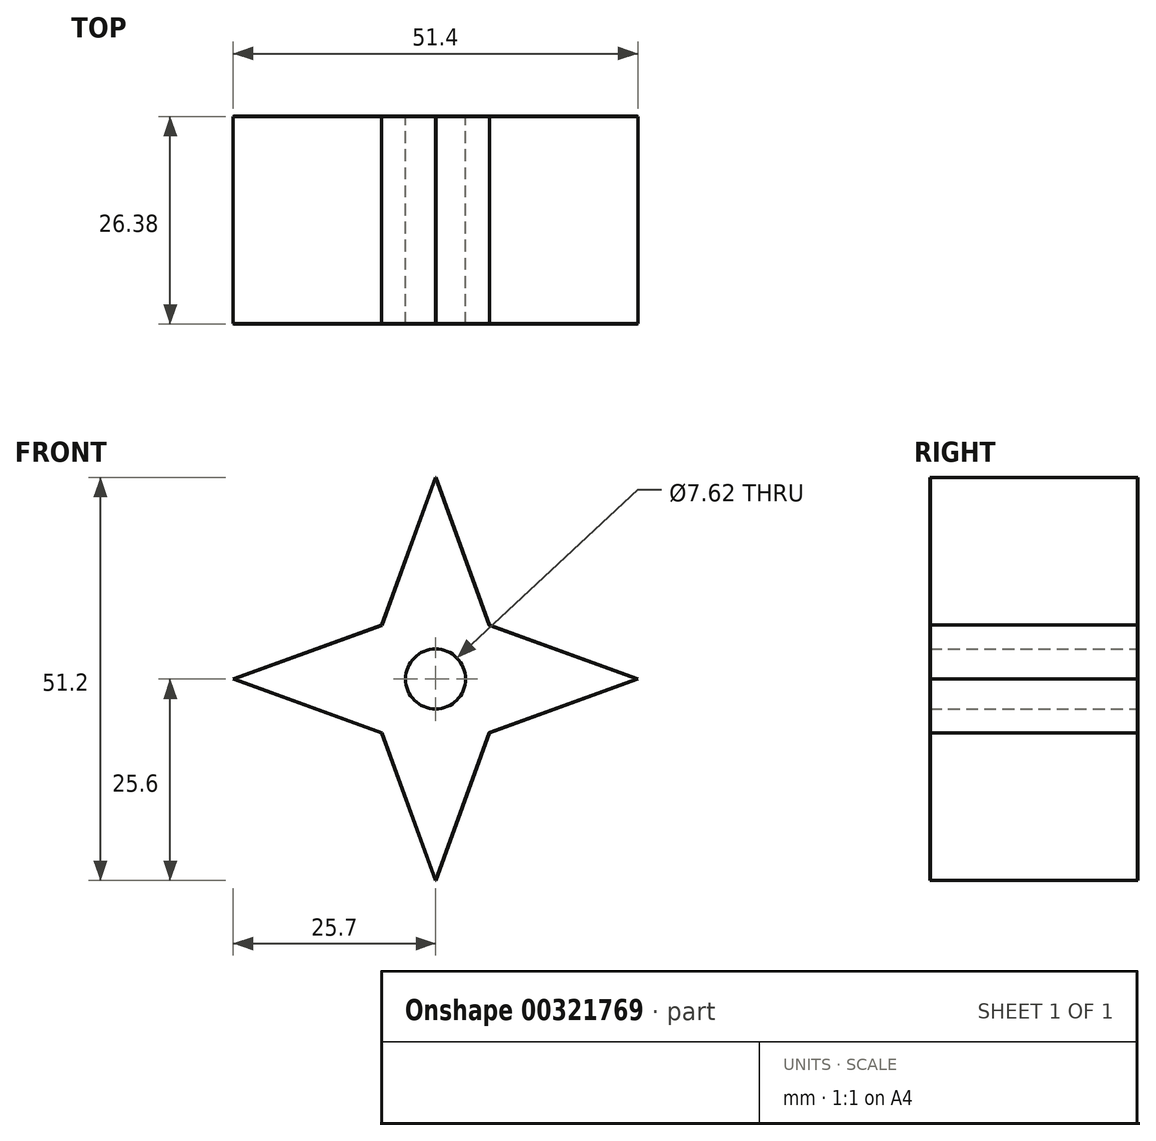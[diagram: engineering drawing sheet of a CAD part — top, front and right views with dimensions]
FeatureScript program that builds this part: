
annotation { "Feature Type Name" : "Feature", "Feature Type Description" : "" }
export const myFeature = defineFeature(function(context is Context, id is Id, definition is map)
    precondition{}
    {
        {
            assignVariable(context, id + "F0", {"name" : "m", "anyValue" : .1});
        }
        {
            var Q0;
            Q0=qCreatedBy(makeId("Front.planeOp"),FACE);
            var sketch = newSketch(context, id + "F1", { "sketchPlane" : qUnion([Q0])});
            skCircle(sketch, "E0.cCircle", {"center": v(0, 0) * mm, "radius": 25.7 * mm, "construction": true});
            skLineSegment(sketch, "E0.0", {"start": v(0, 25.7) * mm, "end": v(25.7, 0) * mm, "construction": true});
            skLineSegment(sketch, "E0.1", {"start": v(25.7, 0) * mm, "end": v(0, -25.7) * mm, "construction": true});
            skLineSegment(sketch, "E0.2", {"start": v(0, -25.7) * mm, "end": v(-25.7, 0) * mm, "construction": true});
            skLineSegment(sketch, "E0.3", {"start": v(-25.7, 0) * mm, "end": v(0, 25.7) * mm, "construction": true});
            skLineSegment(sketch, "E1", {"start": v(-25.7, 0) * mm, "end": v(-6.86, 6.86) * mm});
            skLineSegment(sketch, "E2", {"start": v(-6.86, 6.86) * mm, "end": v(0, 25.7) * mm});
            skLineSegment(sketch, "E3", {"start": v(6.86, 6.86) * mm, "end": v(0, 25.7) * mm});
            skLineSegment(sketch, "E4", {"start": v(6.86, 6.86) * mm, "end": v(25.7, 0) * mm});
            skLineSegment(sketch, "E5", {"start": v(25.7, 0) * mm, "end": v(6.86, -6.86) * mm});
            skLineSegment(sketch, "E6", {"start": v(6.86, -6.86) * mm, "end": v(0, -25.7) * mm});
            skLineSegment(sketch, "E7", {"start": v(0, -25.7) * mm, "end": v(-6.86, -6.86) * mm});
            skLineSegment(sketch, "E8", {"start": v(-6.86, -6.86) * mm, "end": v(-25.7, 0) * mm});
            skCircle(sketch, "E9", {"center": v(0, 0) * mm, "radius": 3.81 * mm});
            skLineSegment(sketch, "E10", {"start": v(-6.86, -6.86) * mm, "end": v(-6.86, 6.86) * mm, "construction": true});
            skLineSegment(sketch, "E11", {"start": v(-6.86, 6.86) * mm, "end": v(6.86, 6.86) * mm, "construction": true});
            skLineSegment(sketch, "E12", {"start": v(6.86, 6.86) * mm, "end": v(6.86, -6.86) * mm, "construction": true});
            skLineSegment(sketch, "E13", {"start": v(-6.86, -6.86) * mm, "end": v(6.86, -6.86) * mm, "construction": true});
            skSolve(sketch);
        }
        {
            var Q0;
            Q0 = qSketchRegion(id + "F1", true);
            extrude(context, id + "F2", {"entities" : qUnion([Q0]), "depth" : getVariable(context, 'm') * 20 * mm});
        }
        {
            var Q0;
            Q0 = qSketchRegion(id + "F1", true);
            extrude(context, id + "F3", {"entities" : qUnion([Q0]), "operationType" : NewBodyOperationType.ADD, "depth" : getVariable(context, 'm') * -243.84 * mm});
        }
        {
            var Q0;
            Q0=makeQuery(id+"F3.opExtrude","CAP_EDGE",EDGE,{"disambiguationData":[OSD([sQuery(id+"F1.wireOp",EDGE,"E2")])],"isStart":false});
            var Q1;
            Q1=makeQuery(id+"F2.opExtrude","CAP_EDGE",EDGE,{"disambiguationData":[OSD([sQuery(id+"F1.wireOp",EDGE,"E2")])],"isStart":false});
            var Q2;
            Q2=makeQuery(id+"F3.opExtrude","CAP_EDGE",EDGE,{"disambiguationData":[OSD([sQuery(id+"F1.wireOp",EDGE,"E1")])],"isStart":false});
            var Q3;
            Q3=makeQuery(id+"F2.opExtrude","CAP_EDGE",EDGE,{"disambiguationData":[OSD([sQuery(id+"F1.wireOp",EDGE,"E1")])],"isStart":false});
            var Q4;
            Q4=makeQuery(id+"F3.opExtrude","CAP_EDGE",EDGE,{"disambiguationData":[OSD([sQuery(id+"F1.wireOp",EDGE,"E8")])],"isStart":false});
            var Q5;
            Q5=makeQuery(id+"F2.opExtrude","CAP_EDGE",EDGE,{"disambiguationData":[OSD([sQuery(id+"F1.wireOp",EDGE,"E8")])],"isStart":false});
            var Q6;
            Q6=makeQuery(id+"F3.opExtrude","CAP_EDGE",EDGE,{"disambiguationData":[OSD([sQuery(id+"F1.wireOp",EDGE,"E7")])],"isStart":false});
            var Q7;
            Q7=makeQuery(id+"F2.opExtrude","CAP_EDGE",EDGE,{"disambiguationData":[OSD([sQuery(id+"F1.wireOp",EDGE,"E7")])],"isStart":false});
            var Q8;
            {var subQ0=sQuery(id+"F1.wireOp",EDGE,"E6");Q8=makeQuery(id+"F3.boolean.opBoolean","MERGE",FACE,{"derivedFrom":[makeQuery(id+"F2.opExtrude","SWEPT_FACE",FACE,{"disambiguationData":[OSD([subQ0])]}),makeQuery(id+"F3.opExtrude","SWEPT_FACE",FACE,{"disambiguationData":[OSD([subQ0])]})]});}
            var Q9;
            {var subQ0=sQuery(id+"F1.wireOp",EDGE,"E3");Q9=makeQuery(id+"F3.boolean.opBoolean","MERGE",FACE,{"derivedFrom":[makeQuery(id+"F2.opExtrude","SWEPT_FACE",FACE,{"disambiguationData":[OSD([subQ0])]}),makeQuery(id+"F3.opExtrude","SWEPT_FACE",FACE,{"disambiguationData":[OSD([subQ0])]})]});}
            chamfer(context, id + "F4", {"entities" : qUnion([Q0, Q1, Q2, Q3, Q4, Q5, Q6, Q7, Q8, Q9]), "width" : (getVariable(context, 'm') * .4) * mm, "tangentPropagation" : true});
        }
    });
